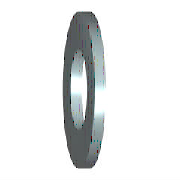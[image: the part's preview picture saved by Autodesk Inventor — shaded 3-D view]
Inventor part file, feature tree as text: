
AUTODESK INVENTOR PART (.ipt)
format: ipt  version: 2019 (Build 230136000, 136)  size: 110,592 bytes
history: native  units: mm (DEFAULTED — no unit token found)
features: other x1, plane x1, sketch x1
ambient origin geometry x7: Origin, YZ Plane, XY Plane, X Axis, Y Axis, Z Axis, Center Point
bodies: Solid1 (feature_tree), Body (feature_tree)
feature tree (3):
  other  "Work Axis1"
  plane  "Work Plane1"
  sketch  "Sketch"  dims[d0=5.3mm d1=10.0mm d2=1.0mm d3=0.0mm d4=0.0mm d5=0.0mm d6=0.0mm d7=0.0mm]
